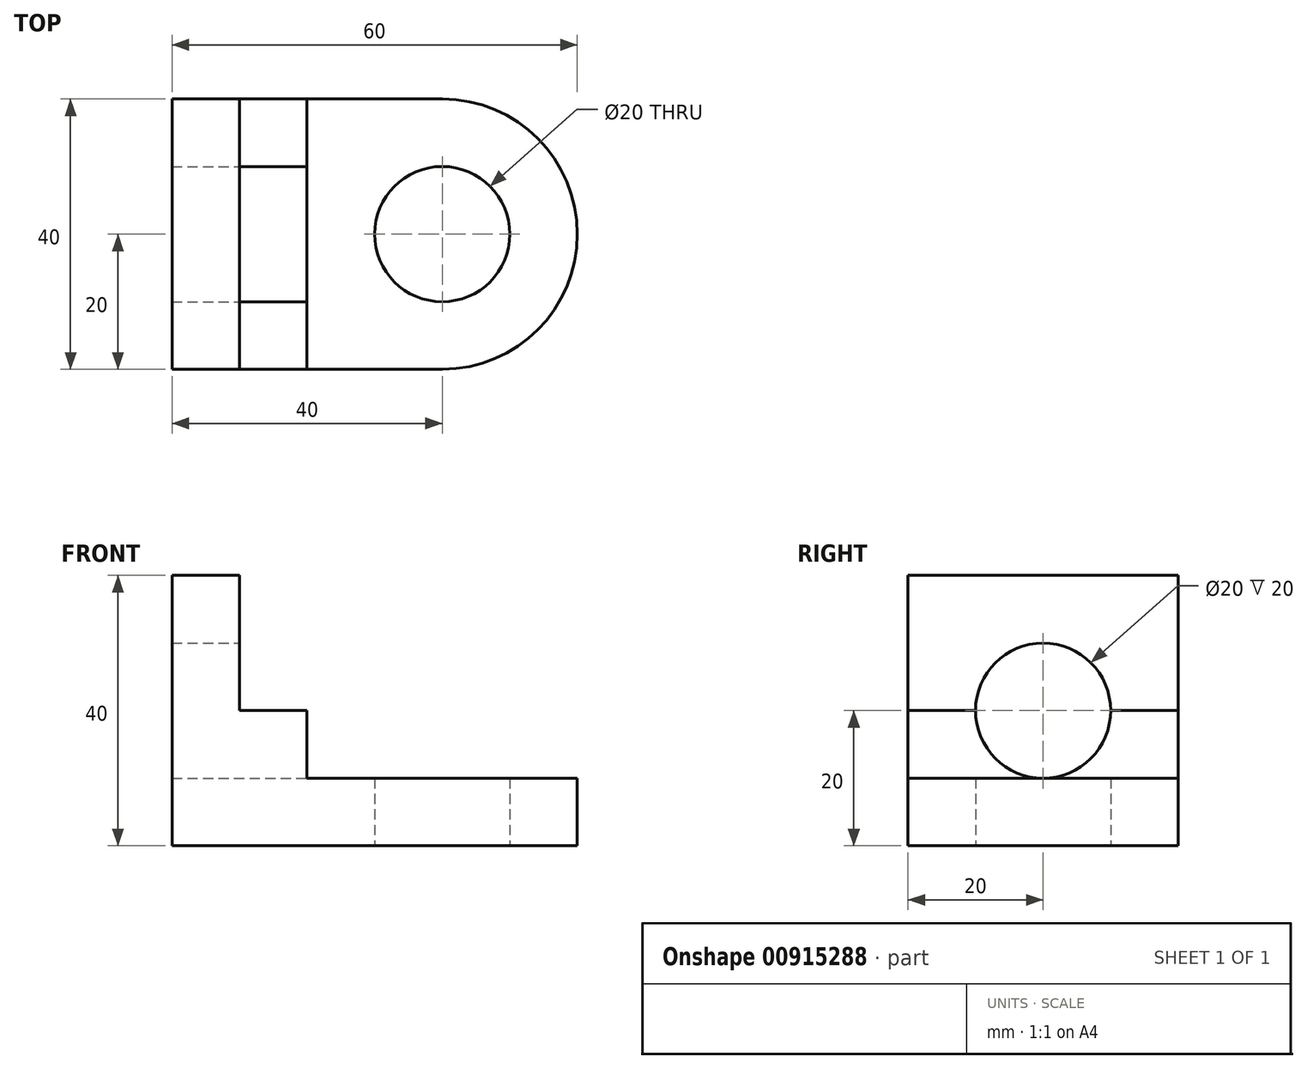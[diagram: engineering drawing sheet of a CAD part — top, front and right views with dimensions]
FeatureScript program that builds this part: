
annotation { "Feature Type Name" : "Feature", "Feature Type Description" : "" }
export const myFeature = defineFeature(function(context is Context, id is Id, definition is map)
    precondition{}
    {
        {
            var Q0;
            Q0=qCreatedBy(makeId("Top.planeOp"),FACE);
            var sketch = newSketch(context, id + "F0", { "sketchPlane" : qUnion([Q0])});
            skLineSegment(sketch, "E0.bottom", {"start": v(0, 0) * mm, "end": v(40, 0) * mm});
            skLineSegment(sketch, "E0.top", {"start": v(0, 40) * mm, "end": v(40, 40) * mm});
            skLineSegment(sketch, "E0.left", {"start": v(0, 0) * mm, "end": v(0, 40) * mm});
            skArc(sketch, "E1", {"start": v(40, 0) * mm, "mid": v(60, 20) * mm, "end": v(40, 40) * mm});
            skCircle(sketch, "E2", {"center": v(40, 20) * mm, "radius": 10 * mm});
            skLineSegment(sketch, "E3", {"start": v(10, 0) * mm, "end": v(10, 40) * mm});
            skLineSegment(sketch, "E4", {"start": v(20, 0) * mm, "end": v(20, 40) * mm});
            skSolve(sketch);
        }
        {
            var Q0;
            {var subQ0=sQuery(id+"F0.wireOp",EDGE,"E0.left");Q0=makeQuery(id+"F0.imprint","IMPRINT",FACE,{"disambiguationData":[TD([[makeQuery(id+"F0.imprint","IMPRINT",EDGE,{"derivedFrom":subQ0}),-1.0]])]});}
            extrude(context, id + "F1", {"entities" : qUnion([Q0]), "depth" : 40 * mm, "offsetDistance" : 25 * mm});
        }
        {
            var Q0;
            {var subQ0=sQuery(id+"F0.wireOp",EDGE,"E3");Q0=makeQuery(id+"F0.imprint","IMPRINT",FACE,{"disambiguationData":[TD([[makeQuery(id+"F0.imprint","IMPRINT",EDGE,{"derivedFrom":subQ0}),-1.0]])]});}
            extrude(context, id + "F2", {"entities" : qUnion([Q0]), "operationType" : NewBodyOperationType.ADD, "depth" : 20 * mm, "offsetDistance" : 25 * mm});
        }
        {
            var Q0;
            {var subQ0=sQuery(id+"F0.wireOp",EDGE,"E1");Q0=makeQuery(id+"F0.imprint","IMPRINT",FACE,{"disambiguationData":[TD([[makeQuery(id+"F0.imprint","IMPRINT",EDGE,{"derivedFrom":subQ0}),1.0]])]});}
            extrude(context, id + "F3", {"entities" : qUnion([Q0]), "operationType" : NewBodyOperationType.ADD, "depth" : 10 * mm, "offsetDistance" : 25 * mm});
        }
        {
            var Q0;
            Q0=makeQuery(id+"F2.opExtrude","SWEPT_FACE",FACE,{"disambiguationData":[OSD([sQuery(id+"F0.wireOp",EDGE,"E4")])]});
            var sketch = newSketch(context, id + "F4", { "sketchPlane" : qUnion([Q0])});
            skLineSegment(sketch, "E5", {"start": v(20, 10) * mm, "end": v(20, 38.26) * mm, "construction": true});
            skCircle(sketch, "E6", {"center": v(20, 20) * mm, "radius": 10 * mm});
            skSolve(sketch);
        }
        {
            var Q0;
            {var subQ0=sQuery(id+"F4.wireOp",EDGE,"E6");var subQ1=sQuery(id+"F0.wireOp",EDGE,"E4");var subQ2=makeQuery(id+"F2.opExtrude","CAP_EDGE",EDGE,{"disambiguationData":[OSD([subQ1])],"isStart":false});var subQ3=makeQuery(id+"F4.imprint","INTERSECT",VERTEX,{"disambiguationData":[OD(0.0)],"derivedFrom":[subQ2,subQ0]});Q0=makeQuery(id+"F4.imprint","IMPRINT",FACE,{"disambiguationData":[TD([[makeQuery(id+"F4.imprint","IMPRINT",EDGE,{"disambiguationData":[TD([[subQ3,-1.0]])],"derivedFrom":subQ0}),1.0]])]});}
            var Q1;
            {var subQ0=sQuery(id+"F4.wireOp",EDGE,"E6");var subQ1=makeQuery(id+"F2.opExtrude","CAP_EDGE",EDGE,{"disambiguationData":[OSD([sQuery(id+"F0.wireOp",EDGE,"E4")])],"isStart":false});var subQ2=makeQuery(id+"F4.imprint","INTERSECT",VERTEX,{"disambiguationData":[OD(0.0)],"derivedFrom":[subQ1,subQ0]});Q1=makeQuery(id+"F4.imprint","IMPRINT",FACE,{"disambiguationData":[TD([[makeQuery(id+"F4.imprint","IMPRINT",EDGE,{"disambiguationData":[TD([[subQ2,1.0]])],"derivedFrom":subQ0}),1.0]])]});}
            extrude(context, id + "F5", {"entities" : qUnion([Q0, Q1]), "operationType" : NewBodyOperationType.REMOVE, "endBound" : BoundingType.THROUGH_ALL, "oppositeDirection" : true, "depth" : 25 * mm, "offsetDistance" : 25 * mm});
        }
    });
